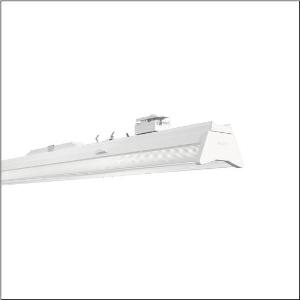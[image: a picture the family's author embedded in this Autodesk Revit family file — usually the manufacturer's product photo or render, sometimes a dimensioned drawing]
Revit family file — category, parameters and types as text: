
# Revit family: licross_21_performance_mo_52td16vn455g
name_source: partatom
category: Lighting Fixtures
units: mm (PartAtom-declared; Revit-internal decimal feet)

## family parameters
Cut with Voids When Loaded = No
Host = Face
Light Source = No
Part Type = Normal
Room Calculation Point = No
Round Connector Dimension = Use Diameter
Shared = No

## types (1)
- --- (1 x LED, 5500 lm, 30 W, 4000K)
    Apparent Load = 30 VA
    CIE Flux Codes = 66 88 96 79 100
    Color Rendering = 80
    Color Temperature = 4000K
    Default Elevation = 1800 mm
    Description = Licross 21 Performance MO, luminaire insert, of sheet steel, galvanised, coil coated, white, length: 1.500mm, width: 120mm, height: 123mm, LED rated luminous flux: 5.500lm, light colour: 840, SDCM (Standard Deviation of Colour Matching)MacAdam ≤ 3 SDCM (initial), control gear: DALI 2, CLO, with plug, 5-pole, with phase selection, mains connection: 220..240V, AC, 50/60Hz, start of lifetime: 30W, end of service life: 36W, internal wiring halogen-free, primary light control with lens, of plastic, primary optical cover: cover, of PMMA, light emission: direct/indirect distribution, primary light characteristic: symmetric, protection rating (complete): IP54, insulation class (complete): insulation class I (protective earthing), certification: CE, ENEC, VDE, UKCA, protection symbol: D if used in an environment with non-conductive dust loads with corresponding accessories, impact resistance: IK06, permissible ambient temperature for indoor applications: -25..+50°C, corresponds to IFS (International Featured Standards) requirements for safety and quality in the food industry, reducing of maximum allowable ambient temperature of 5°C with ceiling mounting, LABS conformity tested according to VDMA 24364:2018-05, The light source and the operating device comply with the requirements of the Ecodesign Regulation (EU) 2019/2020 and are replaceable in accordance with this regulation, packaging unit: 1 piece
    Height = 114 mm
    Lamp = 1 x LED
    Lamp Light Flux = 5500 lm
    Lamp Power = 30 W
    Lamp count = 1
    Length = 1500 mm
    Luminous efficacy = 183 lm/W
    Manufacturer = Siteco
    ModVariant = No
    Model = 52TD16VN455G
    Mounting Place = Ceiling
    Mounting Type = Pendant
    Number of Poles = 1
    OnlyDefault = Yes
    Power Factor = 1
    Product Name = Licross 21 Performance MO
    Product group = luminaire insert | ceiling pendant
    ProductGroupID = 901
    Protection Class = Protection class I
    Protection Degree = IP 54
    RLX_Detail_Level = 1
    RLX_Emergency_Light_Flux = 0 lm
    RLX_Emergency_Type = 0
    RLX_Emergency_Type_DB = No
    RlxData = <blob elided: 33825 chars, md5=3c345d6f>
    Socket = socket
    Standby Power = 0 W
    System Light Flux = 5500 lm
    System Power = 30 W
    Type Comments = factory setting: luminous flux: 100 % | dim-lin: 254 | 203 mA
    Type Image = l_1256138.jpg
    URL = http://relux.com
    VarID = @adj_089549
    Voltage = 0 V
    Weight = 0.00 kg
    Width = 120 mm

## geometry (parser evidence)
native form markers: Blend x4, Sweep x11
no freeform markers — native parametric forms only
